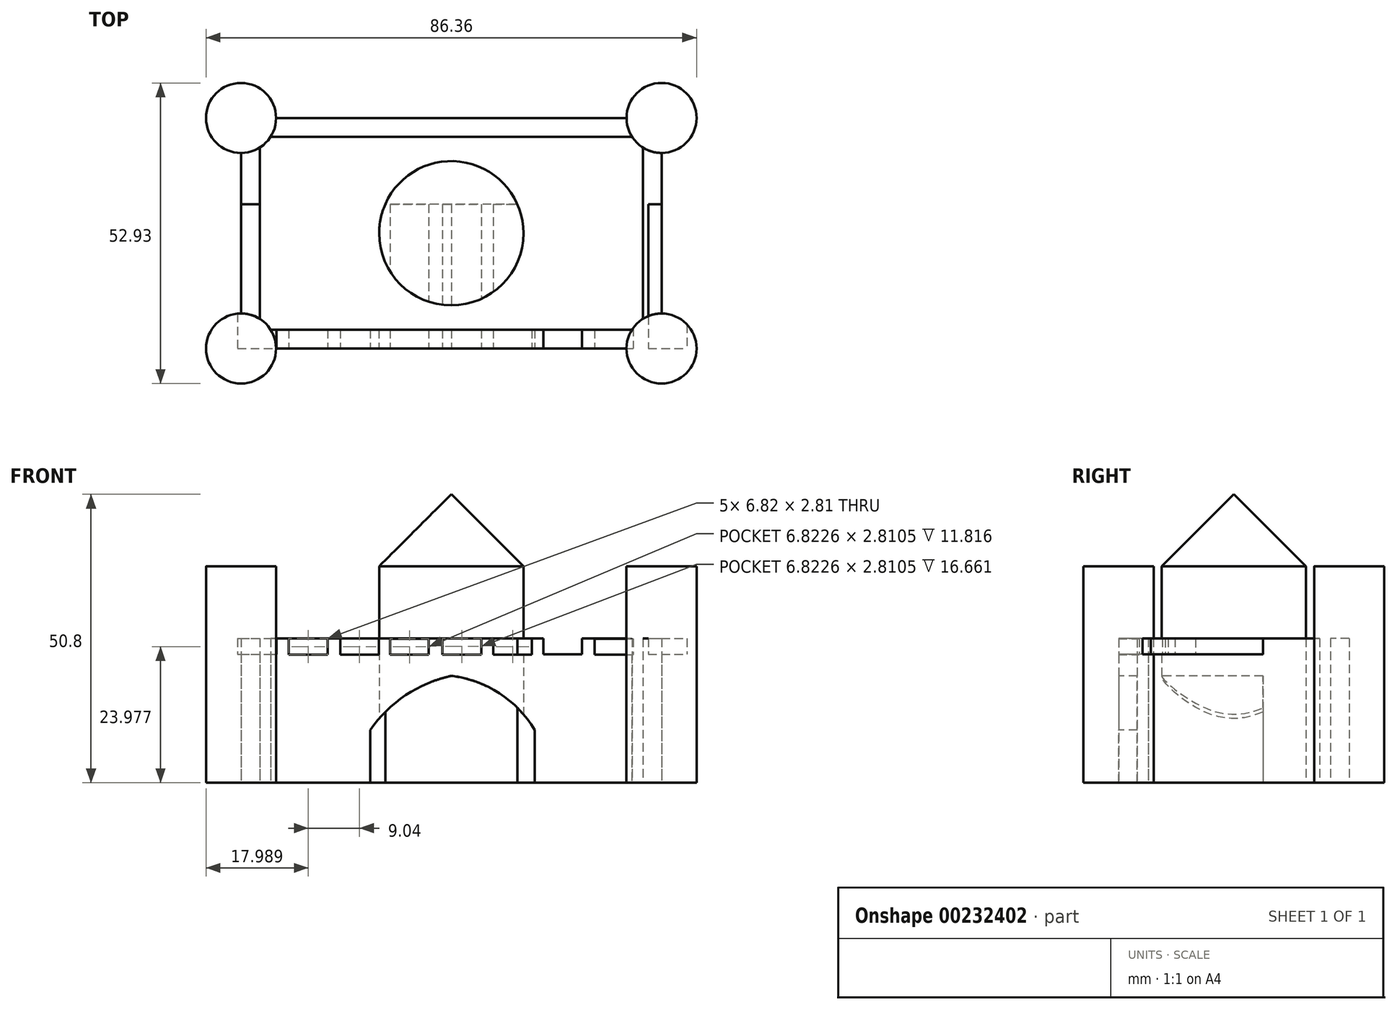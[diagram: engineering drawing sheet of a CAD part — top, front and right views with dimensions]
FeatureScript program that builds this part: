
annotation { "Feature Type Name" : "Feature", "Feature Type Description" : "" }
export const myFeature = defineFeature(function(context is Context, id is Id, definition is map)
    precondition{}
    {
        {
            var Q0;
            Q0=qCreatedBy(makeId("Top.planeOp"),FACE);
            var sketch = newSketch(context, id + "F0", { "sketchPlane" : qUnion([Q0])});
            skLineSegment(sketch, "E0.bottom", {"start": v(30.85, 20.3) * mm, "end": v(-30.85, 20.3) * mm});
            skLineSegment(sketch, "E0.top", {"start": v(30.84, -20.3) * mm, "end": v(-30.84, -20.3) * mm});
            skLineSegment(sketch, "E0.left", {"start": v(37.01, 14.14) * mm, "end": v(37.01, -14.13) * mm});
            skLineSegment(sketch, "E0.right", {"start": v(-37.01, 14.13) * mm, "end": v(-37.01, -14.13) * mm});
            skPoint(sketch, "E0.middle", {"position": v(0, 0) * mm});
            skCircle(sketch, "E1", {"center": v(0, 0) * mm, "radius": 12.7 * mm});
            skCircle(sketch, "E2", {"center": v(-37.01, 20.3) * mm, "radius": 6.17 * mm});
            skCircle(sketch, "E3", {"center": v(37.01, 20.3) * mm, "radius": 6.17 * mm});
            skCircle(sketch, "E4", {"center": v(37, -20.3) * mm, "radius": 6.17 * mm});
            skCircle(sketch, "E5", {"center": v(-37, -20.3) * mm, "radius": 6.17 * mm});
            skLineSegment(sketch, "E6.bottom", {"start": v(31.8, 17) * mm, "end": v(-31.8, 17) * mm});
            skLineSegment(sketch, "E6.top", {"start": v(31.8, -17) * mm, "end": v(-31.8, -17) * mm});
            skLineSegment(sketch, "E6.left", {"start": v(33.73, 15.09) * mm, "end": v(33.73, -15.08) * mm});
            skLineSegment(sketch, "E6.right", {"start": v(-33.73, 15.08) * mm, "end": v(-33.73, -15.07) * mm});
            skPoint(sketch, "E7.orphan", {"position": v(37.01, -20.3) * mm});
            skPoint(sketch, "E8.orphan", {"position": v(33.73, 17) * mm});
            skPoint(sketch, "E9.orphan", {"position": v(33.73, -17) * mm});
            skPoint(sketch, "E10.orphan", {"position": v(-37.01, -20.3) * mm});
            skPoint(sketch, "E11.orphan", {"position": v(-33.73, -17) * mm});
            skPoint(sketch, "E12.orphan", {"position": v(-33.73, 17) * mm});
            skSolve(sketch);
        }
        {
            var Q0;
            {var subQ0=sQuery(id+"F0.wireOp",EDGE,"E0.bottom");Q0=makeQuery(id+"F0.imprint","IMPRINT",FACE,{"disambiguationData":[TD([[makeQuery(id+"F0.imprint","IMPRINT",EDGE,{"derivedFrom":subQ0}),1.0]])]});}
            var Q1;
            {var subQ0=sQuery(id+"F0.wireOp",EDGE,"E0.left");Q1=makeQuery(id+"F0.imprint","IMPRINT",FACE,{"disambiguationData":[TD([[makeQuery(id+"F0.imprint","IMPRINT",EDGE,{"derivedFrom":subQ0}),-1.0]])]});}
            var Q2;
            {var subQ0=sQuery(id+"F0.wireOp",EDGE,"E0.top");Q2=makeQuery(id+"F0.imprint","IMPRINT",FACE,{"disambiguationData":[TD([[makeQuery(id+"F0.imprint","IMPRINT",EDGE,{"derivedFrom":subQ0}),-1.0]])]});}
            var Q3;
            {var subQ0=sQuery(id+"F0.wireOp",EDGE,"E0.right");Q3=makeQuery(id+"F0.imprint","IMPRINT",FACE,{"disambiguationData":[TD([[makeQuery(id+"F0.imprint","IMPRINT",EDGE,{"derivedFrom":subQ0}),1.0]])]});}
            extrude(context, id + "F1", {"entities" : qUnion([Q0, Q1, Q2, Q3]), "depth" : 25.4 * mm});
        }
        {
            var Q0;
            {var subQ0=sQuery(id+"F0.wireOp",EDGE,"E2");var subQ1=makeQuery(id+"F0.imprint","INTERSECT",VERTEX,{"derivedFrom":[sQuery(id+"F0.wireOp",EDGE,"E0.bottom"),subQ0]});Q0=makeQuery(id+"F0.imprint","IMPRINT",FACE,{"disambiguationData":[TD([[makeQuery(id+"F0.imprint","IMPRINT",EDGE,{"disambiguationData":[TD([[subQ1,-1.0]])],"derivedFrom":subQ0}),1.0]])]});}
            var Q1;
            {var subQ0=sQuery(id+"F0.wireOp",EDGE,"E3");var subQ1=makeQuery(id+"F0.imprint","INTERSECT",VERTEX,{"derivedFrom":[sQuery(id+"F0.wireOp",EDGE,"E0.bottom"),subQ0]});Q1=makeQuery(id+"F0.imprint","IMPRINT",FACE,{"disambiguationData":[TD([[makeQuery(id+"F0.imprint","IMPRINT",EDGE,{"disambiguationData":[TD([[subQ1,-1.0]])],"derivedFrom":subQ0}),1.0]])]});}
            var Q2;
            {var subQ0=sQuery(id+"F0.wireOp",EDGE,"E4");var subQ1=makeQuery(id+"F0.imprint","INTERSECT",VERTEX,{"derivedFrom":[sQuery(id+"F0.wireOp",EDGE,"E0.left"),subQ0]});Q2=makeQuery(id+"F0.imprint","IMPRINT",FACE,{"disambiguationData":[TD([[makeQuery(id+"F0.imprint","IMPRINT",EDGE,{"disambiguationData":[TD([[subQ1,-1.0]])],"derivedFrom":subQ0}),1.0]])]});}
            var Q3;
            {var subQ0=sQuery(id+"F0.wireOp",EDGE,"E5");var subQ1=makeQuery(id+"F0.imprint","INTERSECT",VERTEX,{"derivedFrom":[sQuery(id+"F0.wireOp",EDGE,"E0.top"),subQ0]});Q3=makeQuery(id+"F0.imprint","IMPRINT",FACE,{"disambiguationData":[TD([[makeQuery(id+"F0.imprint","IMPRINT",EDGE,{"disambiguationData":[TD([[subQ1,-1.0]])],"derivedFrom":subQ0}),1.0]])]});}
            extrude(context, id + "F2", {"entities" : qUnion([Q0, Q1, Q2, Q3]), "depth" : 38.1 * mm});
        }
        {
            var Q0;
            Q0=makeQuery(id+"F0.imprint","IMPRINT",FACE,{"disambiguationData":[TD([[makeQuery(id+"F0.imprint","IMPRINT",EDGE,{"derivedFrom":sQuery(id+"F0.wireOp",EDGE,"E1")}),1.0]])]});
            extrude(context, id + "F3", {"entities" : qUnion([Q0]), "depth" : 50.8 * mm});
        }
        {
            var Q0;
            Q0=makeQuery(id+"F1.opExtrude","SWEPT_FACE",FACE,{"disambiguationData":[OSD([sQuery(id+"F0.wireOp",EDGE,"E0.top")])]});
            var sketch = newSketch(context, id + "F4", { "sketchPlane" : qUnion([Q0])});
            skLineSegment(sketch, "E13.bottom", {"start": v(-14.27, 0) * mm, "end": v(14.68, 0) * mm});
            skLineSegment(sketch, "E13.left", {"start": v(-14.27, 0) * mm, "end": v(-14.27, 9.3) * mm});
            skLineSegment(sketch, "E13.right", {"start": v(14.68, 0) * mm, "end": v(14.68, 9.3) * mm});
            skArc(sketch, "E14", {"start": v(0, 18.81) * mm, "mid": v(-8.03, 15.4) * mm, "end": v(-14.27, 9.3) * mm});
            skArc(sketch, "E15", {"start": v(14.68, 9.3) * mm, "mid": v(8.44, 15.76) * mm, "end": v(0, 18.81) * mm});
            skLineSegment(sketch, "E16.bottom", {"start": v(-37.6, 25.4) * mm, "end": v(-30.78, 25.4) * mm});
            skLineSegment(sketch, "E16.top", {"start": v(-37.6, 22.59) * mm, "end": v(-30.78, 22.59) * mm});
            skLineSegment(sketch, "E16.left", {"start": v(-37.6, 25.4) * mm, "end": v(-37.6, 22.59) * mm});
            skLineSegment(sketch, "E16.right", {"start": v(-30.78, 25.4) * mm, "end": v(-30.78, 22.59) * mm});
            skLineSegment(sketch, "E17.bottom", {"start": v(-28.6, 25.38) * mm, "end": v(-21.78, 25.38) * mm});
            skLineSegment(sketch, "E17.top", {"start": v(-28.6, 22.57) * mm, "end": v(-21.78, 22.57) * mm});
            skLineSegment(sketch, "E17.left", {"start": v(-28.6, 25.38) * mm, "end": v(-28.6, 22.57) * mm});
            skLineSegment(sketch, "E17.right", {"start": v(-21.78, 25.38) * mm, "end": v(-21.78, 22.57) * mm});
            skLineSegment(sketch, "E18.bottom", {"start": v(-19.56, 25.38) * mm, "end": v(-12.74, 25.38) * mm});
            skLineSegment(sketch, "E18.top", {"start": v(-19.56, 22.57) * mm, "end": v(-12.74, 22.57) * mm});
            skLineSegment(sketch, "E18.left", {"start": v(-19.56, 25.38) * mm, "end": v(-19.56, 22.57) * mm});
            skLineSegment(sketch, "E18.right", {"start": v(-12.74, 25.38) * mm, "end": v(-12.74, 22.57) * mm});
            skLineSegment(sketch, "E19.bottom", {"start": v(-10.78, 25.34) * mm, "end": v(-3.96, 25.34) * mm});
            skLineSegment(sketch, "E19.top", {"start": v(-10.78, 22.53) * mm, "end": v(-3.96, 22.53) * mm});
            skLineSegment(sketch, "E19.left", {"start": v(-10.78, 25.34) * mm, "end": v(-10.78, 22.53) * mm});
            skLineSegment(sketch, "E19.right", {"start": v(-3.96, 25.34) * mm, "end": v(-3.96, 22.53) * mm});
            skLineSegment(sketch, "E20.bottom", {"start": v(-1.55, 25.39) * mm, "end": v(5.27, 25.39) * mm});
            skLineSegment(sketch, "E20.top", {"start": v(-1.55, 22.58) * mm, "end": v(5.27, 22.58) * mm});
            skLineSegment(sketch, "E20.left", {"start": v(-1.55, 25.39) * mm, "end": v(-1.55, 22.58) * mm});
            skLineSegment(sketch, "E20.right", {"start": v(5.27, 25.39) * mm, "end": v(5.27, 22.58) * mm});
            skLineSegment(sketch, "E21.bottom", {"start": v(7.38, 25.38) * mm, "end": v(14.2, 25.38) * mm});
            skLineSegment(sketch, "E21.top", {"start": v(7.38, 22.57) * mm, "end": v(14.2, 22.57) * mm});
            skLineSegment(sketch, "E21.left", {"start": v(7.38, 25.38) * mm, "end": v(7.38, 22.57) * mm});
            skLineSegment(sketch, "E21.right", {"start": v(14.2, 25.38) * mm, "end": v(14.2, 22.57) * mm});
            skLineSegment(sketch, "E22.bottom", {"start": v(16.19, 25.4) * mm, "end": v(23.01, 25.4) * mm});
            skLineSegment(sketch, "E22.top", {"start": v(16.19, 22.59) * mm, "end": v(23.01, 22.59) * mm});
            skLineSegment(sketch, "E22.left", {"start": v(16.19, 25.4) * mm, "end": v(16.19, 22.59) * mm});
            skLineSegment(sketch, "E22.right", {"start": v(23.01, 25.4) * mm, "end": v(23.01, 22.59) * mm});
            skLineSegment(sketch, "E23.bottom", {"start": v(25.22, 25.37) * mm, "end": v(32.05, 25.37) * mm});
            skLineSegment(sketch, "E23.top", {"start": v(25.22, 22.56) * mm, "end": v(32.05, 22.56) * mm});
            skLineSegment(sketch, "E23.left", {"start": v(25.22, 25.37) * mm, "end": v(25.22, 22.56) * mm});
            skLineSegment(sketch, "E23.right", {"start": v(32.05, 25.37) * mm, "end": v(32.05, 22.56) * mm});
            skLineSegment(sketch, "E24.bottom", {"start": v(34.68, 25.4) * mm, "end": v(41.5, 25.4) * mm});
            skLineSegment(sketch, "E24.top", {"start": v(34.68, 22.6) * mm, "end": v(41.5, 22.6) * mm});
            skLineSegment(sketch, "E24.left", {"start": v(34.68, 25.4) * mm, "end": v(34.68, 22.6) * mm});
            skLineSegment(sketch, "E24.right", {"start": v(41.5, 25.4) * mm, "end": v(41.5, 22.6) * mm});
            skSolve(sketch);
        }
        {
            var Q0;
            Q0=makeQuery(id+"F4.imprint","IMPRINT",FACE,{"disambiguationData":[TD([[makeQuery(id+"F4.imprint","IMPRINT",EDGE,{"derivedFrom":sQuery(id+"F4.wireOp",EDGE,"E13.bottom")}),-1.0]])]});
            extrude(context, id + "F5", {"entities" : qUnion([Q0]), "operationType" : NewBodyOperationType.REMOVE, "oppositeDirection" : true, "depth" : 25.4 * mm});
        }
        {
            var Q0;
            Q0 = qSketchRegion(id + "F4", true);
            extrude(context, id + "F6", {"entities" : qUnion([Q0]), "operationType" : NewBodyOperationType.REMOVE, "oppositeDirection" : true, "depth" : 25.4 * mm});
        }
        {
            var Q0;
            Q0=makeQuery(id+"F3.opExtrude","CAP_FACE",FACE,{"disambiguationData":[OSD([sQuery(id+"F0.wireOp",EDGE,"E1")])],"isStart":false});
            chamfer(context, id + "F7", {"entities" : qUnion([Q0]), "width" : 12.7 * mm, "tangentPropagation" : true});
        }
    });
